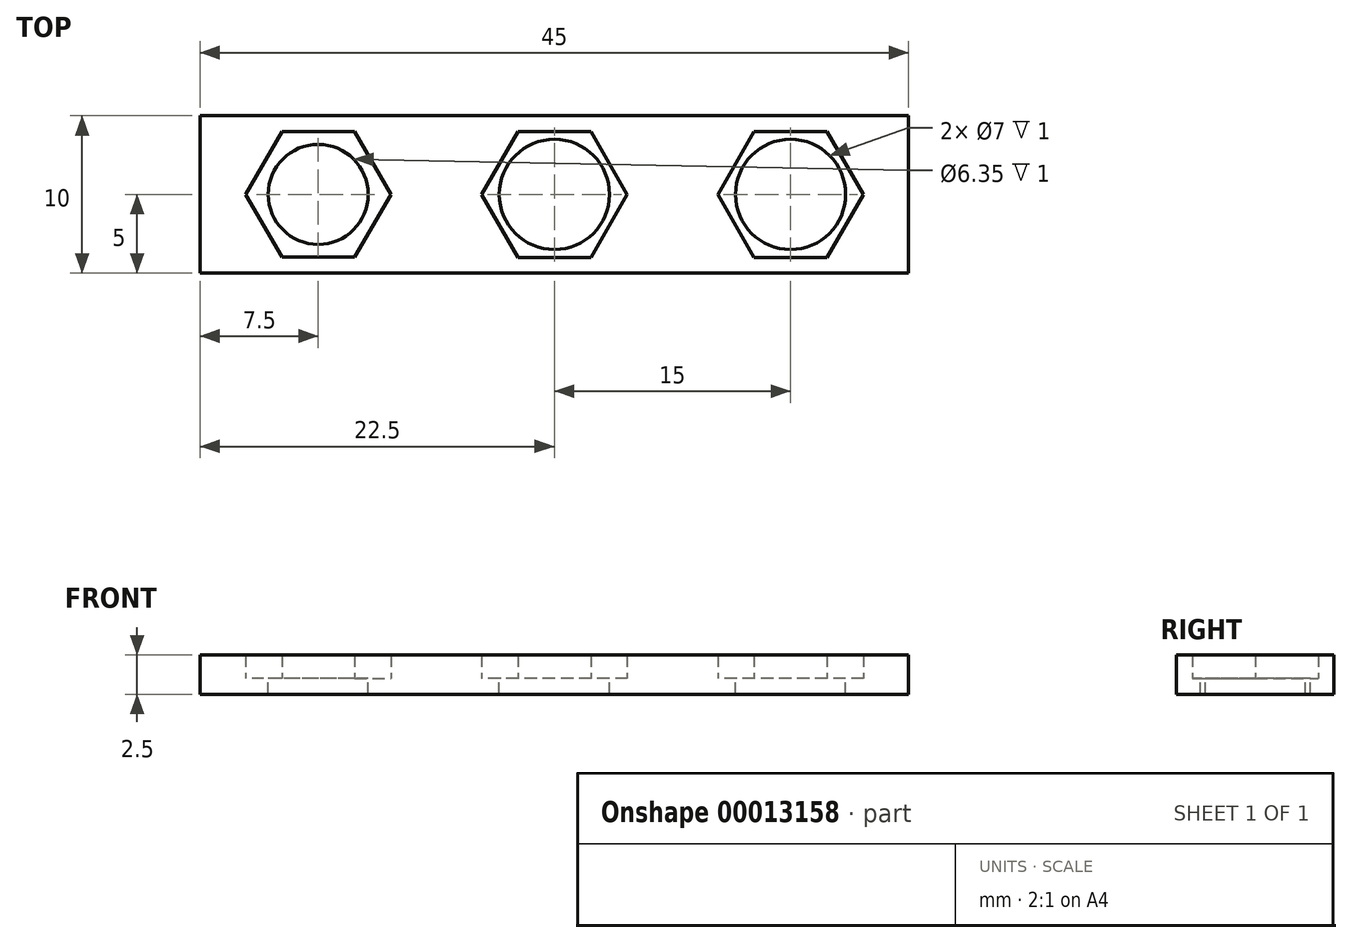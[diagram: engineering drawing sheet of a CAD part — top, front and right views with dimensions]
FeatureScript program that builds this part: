
annotation { "Feature Type Name" : "Feature", "Feature Type Description" : "" }
export const myFeature = defineFeature(function(context is Context, id is Id, definition is map)
    precondition{}
    {
        {
            var Q0;
            Q0=qCreatedBy(makeId("Top.planeOp"),FACE);
            var sketch = newSketch(context, id + "F0", { "sketchPlane" : qUnion([Q0])});
            skLineSegment(sketch, "E0.bottom", {"start": v(-22.5, -5) * mm, "end": v(22.5, -5) * mm});
            skLineSegment(sketch, "E0.top", {"start": v(-22.5, 5) * mm, "end": v(22.5, 5) * mm});
            skLineSegment(sketch, "E0.left", {"start": v(-22.5, -5) * mm, "end": v(-22.5, 5) * mm});
            skLineSegment(sketch, "E0.right", {"start": v(22.5, -5) * mm, "end": v(22.5, 5) * mm});
            skCircle(sketch, "E1.cCircle", {"center": v(0, 0) * mm, "radius": 4 * mm, "construction": true});
            skLineSegment(sketch, "E1.0", {"start": v(2.3, -4) * mm, "end": v(-2.3, -4) * mm});
            skLineSegment(sketch, "E1.1", {"start": v(-2.3, -4) * mm, "end": v(-4.62, 0) * mm});
            skLineSegment(sketch, "E1.2", {"start": v(-4.62, 0) * mm, "end": v(-2.3, 4) * mm});
            skLineSegment(sketch, "E1.3", {"start": v(-2.3, 4) * mm, "end": v(2.3, 4) * mm});
            skLineSegment(sketch, "E1.4", {"start": v(2.3, 4) * mm, "end": v(4.62, 0) * mm});
            skLineSegment(sketch, "E1.5", {"start": v(4.62, 0) * mm, "end": v(2.3, -4) * mm});
            skPoint(sketch, "E1.0.midPoint", {"position": v(0, -4) * mm});
            skCircle(sketch, "E2.cCircle", {"center": v(15, 0) * mm, "radius": 4 * mm, "construction": true});
            skLineSegment(sketch, "E2.0", {"start": v(17.3, -4) * mm, "end": v(12.7, -4) * mm});
            skLineSegment(sketch, "E2.1", {"start": v(12.7, -4) * mm, "end": v(10.38, 0) * mm});
            skLineSegment(sketch, "E2.2", {"start": v(10.38, 0) * mm, "end": v(12.7, 4) * mm});
            skLineSegment(sketch, "E2.3", {"start": v(12.7, 4) * mm, "end": v(17.3, 4) * mm});
            skLineSegment(sketch, "E2.4", {"start": v(17.3, 4) * mm, "end": v(19.62, 0) * mm});
            skLineSegment(sketch, "E2.5", {"start": v(19.62, 0) * mm, "end": v(17.3, -4) * mm});
            skPoint(sketch, "E2.0.midPoint", {"position": v(15, -4) * mm});
            skLineSegment(sketch, "E3.2", {"start": v(-19.62, 0) * mm, "end": v(-17.3, 4) * mm});
            skCircle(sketch, "E3.cCircle", {"center": v(-15, 0) * mm, "radius": 4 * mm, "construction": true});
            skLineSegment(sketch, "E3.0", {"start": v(-12.7, -4) * mm, "end": v(-17.3, -4) * mm});
            skLineSegment(sketch, "E3.3", {"start": v(-17.3, 4) * mm, "end": v(-12.7, 4) * mm});
            skLineSegment(sketch, "E3.1", {"start": v(-17.3, -4) * mm, "end": v(-19.62, 0) * mm});
            skLineSegment(sketch, "E3.4", {"start": v(-12.7, 4) * mm, "end": v(-10.38, 0) * mm});
            skLineSegment(sketch, "E3.5", {"start": v(-10.38, 0) * mm, "end": v(-12.7, -4) * mm});
            skPoint(sketch, "E3.0.midPoint", {"position": v(-15, -4) * mm});
            skSolve(sketch);
        }
        {
            var Q0;
            Q0 = qSketchRegion(id + "F0", true);
            extrude(context, id + "F1", {"entities" : qUnion([Q0]), "depth" : 1.5 * mm});
        }
        {
            var Q0;
            Q0=qCreatedBy(makeId("Top.planeOp"),FACE);
            var sketch = newSketch(context, id + "F2", { "sketchPlane" : qUnion([Q0])});
            skLineSegment(sketch, "E4.bottom", {"start": v(22.5, -5) * mm, "end": v(-22.5, -5) * mm});
            skLineSegment(sketch, "E4.top", {"start": v(22.5, 5) * mm, "end": v(-22.5, 5) * mm});
            skLineSegment(sketch, "E4.left", {"start": v(22.5, -5) * mm, "end": v(22.5, 5) * mm});
            skLineSegment(sketch, "E4.right", {"start": v(-22.5, -5) * mm, "end": v(-22.5, 5) * mm});
            skCircle(sketch, "E5", {"center": v(0, 0) * mm, "radius": 3.5 * mm});
            skCircle(sketch, "E6", {"center": v(-15, 0) * mm, "radius": 3.18 * mm});
            skCircle(sketch, "E7", {"center": v(15, 0) * mm, "radius": 3.5 * mm});
            skSolve(sketch);
        }
        {
            var Q0;
            Q0 = qSketchRegion(id + "F2", true);
            extrude(context, id + "F3", {"entities" : qUnion([Q0]), "operationType" : NewBodyOperationType.ADD, "oppositeDirection" : true, "depth" : 1 * mm});
        }
    });
